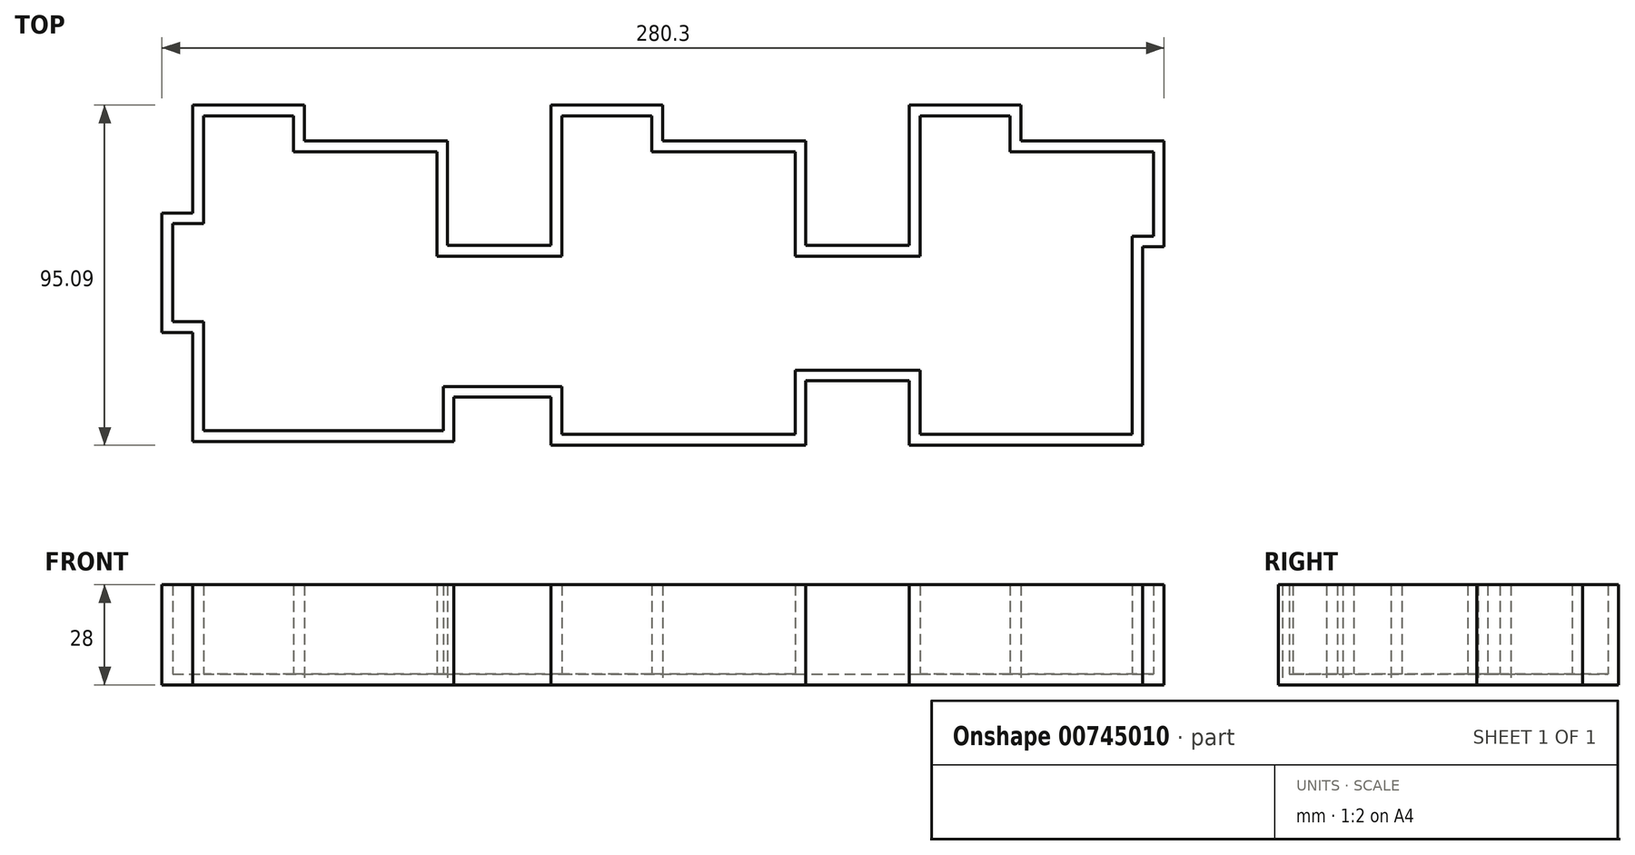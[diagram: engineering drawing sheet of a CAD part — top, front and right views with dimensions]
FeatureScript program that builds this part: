
annotation { "Feature Type Name" : "Feature", "Feature Type Description" : "" }
export const myFeature = defineFeature(function(context is Context, id is Id, definition is map)
    precondition{}
    {
        {
            var Q0;
            Q0=qCreatedBy(makeId("Top.planeOp"),FACE);
            var sketch = newSketch(context, id + "F0", { "sketchPlane" : qUnion([Q0])});
            skLineSegment(sketch, "E0", {"start": v(0, 0) * mm, "end": v(31.2, 0) * mm});
            skLineSegment(sketch, "E1", {"start": v(31.2, 0) * mm, "end": v(31.2, -10) * mm});
            skLineSegment(sketch, "E2", {"start": v(31.2, -10) * mm, "end": v(71.3, -10) * mm});
            skLineSegment(sketch, "E3", {"start": v(71.3, -10) * mm, "end": v(71.3, -39.2) * mm});
            skLineSegment(sketch, "E4", {"start": v(71.3, -39.2) * mm, "end": v(100.2, -39.2) * mm});
            skLineSegment(sketch, "E5", {"start": v(100.2, -39.2) * mm, "end": v(100.2, 0) * mm});
            skLineSegment(sketch, "E6", {"start": v(100.2, 0) * mm, "end": v(131.4, 0) * mm});
            skLineSegment(sketch, "E7", {"start": v(131.4, 0) * mm, "end": v(131.4, -10) * mm});
            skLineSegment(sketch, "E8", {"start": v(131.4, -10) * mm, "end": v(171.5, -10) * mm});
            skLineSegment(sketch, "E9", {"start": v(171.5, -10) * mm, "end": v(171.5, -39.2) * mm});
            skLineSegment(sketch, "E10", {"start": v(171.5, -39.2) * mm, "end": v(200.4, -39.2) * mm});
            skLineSegment(sketch, "E11", {"start": v(200.4, -39.2) * mm, "end": v(200.4, 0) * mm});
            skLineSegment(sketch, "E12", {"start": v(200.4, 0) * mm, "end": v(231.6, 0) * mm});
            skLineSegment(sketch, "E13", {"start": v(231.6, 0) * mm, "end": v(231.6, -10) * mm});
            skLineSegment(sketch, "E14", {"start": v(231.6, -10) * mm, "end": v(271.7, -10) * mm});
            skLineSegment(sketch, "E15", {"start": v(271.7, -10) * mm, "end": v(271.7, -39.6) * mm});
            skLineSegment(sketch, "E16", {"start": v(265.7, -39.6) * mm, "end": v(271.7, -39.6) * mm});
            skLineSegment(sketch, "E17", {"start": v(100.2, -95.09) * mm, "end": v(100.2, -81.66) * mm});
            skLineSegment(sketch, "E18", {"start": v(100.2, -81.66) * mm, "end": v(73.05, -81.66) * mm});
            skLineSegment(sketch, "E19", {"start": v(73.05, -81.66) * mm, "end": v(73.05, -94.04) * mm});
            skLineSegment(sketch, "E20", {"start": v(73.05, -94.04) * mm, "end": v(0, -94.04) * mm});
            skLineSegment(sketch, "E21", {"start": v(0, -94.04) * mm, "end": v(0, -63.58) * mm});
            skLineSegment(sketch, "E22", {"start": v(0, -63.58) * mm, "end": v(-8.6, -63.58) * mm});
            skLineSegment(sketch, "E23", {"start": v(-8.6, -63.58) * mm, "end": v(-8.6, -30.12) * mm});
            skLineSegment(sketch, "E24", {"start": v(-8.6, -30.12) * mm, "end": v(0, -30.12) * mm});
            skLineSegment(sketch, "E25", {"start": v(0, -30.12) * mm, "end": v(0, 0) * mm});
            skLineSegment(sketch, "E26", {"start": v(171.5, -95.09) * mm, "end": v(171.5, -77.06) * mm});
            skLineSegment(sketch, "E27", {"start": v(171.5, -77.06) * mm, "end": v(200.4, -77.06) * mm});
            skLineSegment(sketch, "E28", {"start": v(200.4, -77.06) * mm, "end": v(200.4, -95.09) * mm});
            skLineSegment(sketch, "E29", {"start": v(100.2, -95.09) * mm, "end": v(171.5, -95.09) * mm});
            skLineSegment(sketch, "E30", {"start": v(200.4, -95.09) * mm, "end": v(265.7, -95.09) * mm});
            skLineSegment(sketch, "E31", {"start": v(265.7, -39.6) * mm, "end": v(265.7, -95.09) * mm});
            skSolve(sketch);
        }
        {
            var Q0;
            Q0=makeQuery(id+"F0.imprint","IMPRINT",FACE,{"disambiguationData":[TD([[makeQuery(id+"F0.imprint","IMPRINT",EDGE,{"derivedFrom":sQuery(id+"F0.wireOp",EDGE,"E0")}),-1.0]])]});
            extrude(context, id + "F1", {"entities" : qUnion([Q0]), "depth" : 3 * mm, "offsetDistance" : 25 * mm});
        }
        {
            var Q0;
            Q0=makeQuery(id+"F1.opExtrude","CAP_FACE",FACE,{"disambiguationData":[OSD([sQuery(id+"F0.wireOp",EDGE,"E0"),sQuery(id+"F0.wireOp",EDGE,"E1"),sQuery(id+"F0.wireOp",EDGE,"E2"),sQuery(id+"F0.wireOp",EDGE,"E3"),sQuery(id+"F0.wireOp",EDGE,"E4"),sQuery(id+"F0.wireOp",EDGE,"E5"),sQuery(id+"F0.wireOp",EDGE,"E6"),sQuery(id+"F0.wireOp",EDGE,"E7"),sQuery(id+"F0.wireOp",EDGE,"E8"),sQuery(id+"F0.wireOp",EDGE,"E9"),sQuery(id+"F0.wireOp",EDGE,"E10"),sQuery(id+"F0.wireOp",EDGE,"E11"),sQuery(id+"F0.wireOp",EDGE,"E12"),sQuery(id+"F0.wireOp",EDGE,"E13"),sQuery(id+"F0.wireOp",EDGE,"E14"),sQuery(id+"F0.wireOp",EDGE,"E15"),sQuery(id+"F0.wireOp",EDGE,"E16"),sQuery(id+"F0.wireOp",EDGE,"E17"),sQuery(id+"F0.wireOp",EDGE,"E18"),sQuery(id+"F0.wireOp",EDGE,"E19"),sQuery(id+"F0.wireOp",EDGE,"E20"),sQuery(id+"F0.wireOp",EDGE,"E21"),sQuery(id+"F0.wireOp",EDGE,"E22"),sQuery(id+"F0.wireOp",EDGE,"E23"),sQuery(id+"F0.wireOp",EDGE,"E24"),sQuery(id+"F0.wireOp",EDGE,"E25"),sQuery(id+"F0.wireOp",EDGE,"E26"),sQuery(id+"F0.wireOp",EDGE,"E27"),sQuery(id+"F0.wireOp",EDGE,"E28"),sQuery(id+"F0.wireOp",EDGE,"E29"),sQuery(id+"F0.wireOp",EDGE,"E30"),sQuery(id+"F0.wireOp",EDGE,"E31")])],"isStart":false});
            var sketch = newSketch(context, id + "F2", { "sketchPlane" : qUnion([Q0])});
            skLineSegment(sketch, "E32.0", {"start": v(3, -60.58) * mm, "end": v(3, -91.04) * mm});
            skLineSegment(sketch, "E32.1", {"start": v(-5.6, -60.58) * mm, "end": v(3, -60.58) * mm});
            skLineSegment(sketch, "E32.2", {"start": v(-5.6, -33.12) * mm, "end": v(-5.6, -60.58) * mm});
            skLineSegment(sketch, "E32.3", {"start": v(3, -33.12) * mm, "end": v(-5.6, -33.12) * mm});
            skLineSegment(sketch, "E32.4", {"start": v(3, -3) * mm, "end": v(3, -33.12) * mm});
            skLineSegment(sketch, "E32.5", {"start": v(28.2, -3) * mm, "end": v(3, -3) * mm});
            skLineSegment(sketch, "E32.6", {"start": v(28.2, -13) * mm, "end": v(28.2, -3) * mm});
            skLineSegment(sketch, "E32.7", {"start": v(68.3, -13) * mm, "end": v(28.2, -13) * mm});
            skLineSegment(sketch, "E32.8", {"start": v(68.3, -42.2) * mm, "end": v(68.3, -13) * mm});
            skLineSegment(sketch, "E32.9", {"start": v(262.7, -36.6) * mm, "end": v(268.7, -36.6) * mm});
            skLineSegment(sketch, "E32.10", {"start": v(262.7, -92.09) * mm, "end": v(262.7, -36.6) * mm});
            skLineSegment(sketch, "E32.11", {"start": v(203.4, -92.09) * mm, "end": v(262.7, -92.09) * mm});
            skLineSegment(sketch, "E32.12", {"start": v(203.4, -74.06) * mm, "end": v(203.4, -92.09) * mm});
            skLineSegment(sketch, "E32.13", {"start": v(168.5, -74.06) * mm, "end": v(203.4, -74.06) * mm});
            skLineSegment(sketch, "E32.14", {"start": v(168.5, -92.09) * mm, "end": v(168.5, -74.06) * mm});
            skLineSegment(sketch, "E32.15", {"start": v(70.05, -91.04) * mm, "end": v(70.05, -78.66) * mm});
            skLineSegment(sketch, "E32.16", {"start": v(70.05, -78.66) * mm, "end": v(103.2, -78.66) * mm});
            skLineSegment(sketch, "E32.17", {"start": v(103.2, -78.66) * mm, "end": v(103.2, -92.09) * mm});
            skLineSegment(sketch, "E32.18", {"start": v(103.2, -92.09) * mm, "end": v(168.5, -92.09) * mm});
            skLineSegment(sketch, "E32.19", {"start": v(268.7, -36.6) * mm, "end": v(268.7, -13) * mm});
            skLineSegment(sketch, "E32.20", {"start": v(268.7, -13) * mm, "end": v(228.6, -13) * mm});
            skLineSegment(sketch, "E32.21", {"start": v(228.6, -13) * mm, "end": v(228.6, -3) * mm});
            skLineSegment(sketch, "E32.22", {"start": v(228.6, -3) * mm, "end": v(203.4, -3) * mm});
            skLineSegment(sketch, "E32.23", {"start": v(203.4, -3) * mm, "end": v(203.4, -42.2) * mm});
            skLineSegment(sketch, "E32.24", {"start": v(203.4, -42.2) * mm, "end": v(168.5, -42.2) * mm});
            skLineSegment(sketch, "E32.25", {"start": v(168.5, -42.2) * mm, "end": v(168.5, -13) * mm});
            skLineSegment(sketch, "E32.26", {"start": v(168.5, -13) * mm, "end": v(128.4, -13) * mm});
            skLineSegment(sketch, "E32.27", {"start": v(128.4, -13) * mm, "end": v(128.4, -3) * mm});
            skLineSegment(sketch, "E32.28", {"start": v(3, -91.04) * mm, "end": v(70.05, -91.04) * mm});
            skLineSegment(sketch, "E32.29", {"start": v(128.4, -3) * mm, "end": v(103.2, -3) * mm});
            skLineSegment(sketch, "E32.30", {"start": v(103.2, -3) * mm, "end": v(103.2, -42.2) * mm});
            skLineSegment(sketch, "E32.31", {"start": v(103.2, -42.2) * mm, "end": v(68.3, -42.2) * mm});
            skSolve(sketch);
        }
        {
            var Q0;
            Q0=makeQuery(id+"F2.imprint","IMPRINT",FACE,{"disambiguationData":[TD([[makeQuery(id+"F2.imprint","IMPRINT",EDGE,{"derivedFrom":sQuery(id+"F2.wireOp",EDGE,"E32.0")}),-1.0]])]});
            extrude(context, id + "F3", {"entities" : qUnion([Q0]), "operationType" : NewBodyOperationType.ADD, "depth" : 25 * mm, "offsetDistance" : 25 * mm});
        }
    });
